# Revit family: IS_Ceratherm50_A6368_BIM_FR
name_source: partatom
category: Plumbing Fixtures
revit_build: Autodesk Revit 2017 (Build: 20160225_1515(x64)
units: mm (PartAtom-declared; Revit-internal decimal feet)

## family parameters
Always vertical = No
Cut with Voids When Loaded = No
OmniClass Number = 23.45.05.17
OmniClass Title = Sanitary Leisure Units
Part Type = Normal
Room Calculation Point = No
Round Connector Dimension = Use Diameter
Shared = No
Work Plane-Based = No

## types (1)
- A6368AA - IDEALRAIN COMBI  DCH TH  L3 3J  90 1,75M CH
    Accessoires = www.idealspec.fr
    Auteur = Ideal Standard
    BIMobject category = Showers
    BIMobject category code = sanitary-showers
    BIMobject main category = Sanitary
    BIMobject main category code = sanitary
    BOSUseNativeGeometries = 1
    Bim-NomDuProjet = ISI_IdealStandard_ShowerHeads_IDEALRAIN_A6368AA
    Brand url = www.idealspec.fr
    Caractéristiques = IDEALRAIN SHR EXP &KIT/I'R 3F 900 NEW
    CodeBarre = 4015413334525
    Conformité = NF
    ConseilsDInstallation = 0
    Cost = 0 $
    Couleur = Chrome
    CoûtDeRemplacement = 0
    Date of publishing = 2018_07_24
    DateDeCréation = 2018_07_24
    Description = IDEALRAIN Ensemble de douche thermostatique
    Dimensions = 1104 x 188 x 436 mm
    EAN code = https://4015413334525
    Edition number = 1
    Espace = Interne
    Finition = Chrome
    Forme = Complexe
    Hauteur = 1104 mm
    IFC Classification = Sanitary Terminal
    IfcExportAs = SHOWERS
    IfcExportType = IfcValveType
    InformationsProduit = www.idealspec.fr
    Installation instructions = http://www.idealspec.fr
    Largeur = 188 mm
    Longueur = 436 mm
    Manufacturer name = Ideal Standard
    Marque = Ideal Standard
    Material main = Brass
    Matériel = Brass
    Model = A6368AA
    NBS Reference Code = 35-06-81
    NBS Reference Description = Shower Heads
    Nominal height = 904
    Nominal width = 304
    OmniClass Code = 23-31 17 00
    OmniClass Description = Showers
    Product Guid = 17cbef67-e42c-4ce9-9d03-9a8c88c3f477
    Product SKU = A6368
    Product certification = http://www.idealspec.fr
    Product data url = https://bimobject.com
    Product family = IDEALRAIN
    Product group = Shower
    Product name = IDEALRAIN SHR EXP &KIT/I'R 3F 900 NEW
    Product url = http://www.idealspec.fr
    Profondeur = 0 mm  [stored 0 ft]
    QR code = http://bimobject.com
    Raccordement = Plomberie
    Révision = 1
    Technical description = http://www.idealspec.fr
    TestDePression = 0
    TypeDeRobinetterie = Shower Mixer
    URL = www.idealspec.fr
    Uniclass 1.4 Code = L7214
    Uniclass 1.4 Description = Showers
    Uniclass 2.0 Code = PR-35-06-81
    Uniclass 2.0 Description = Shower Heads
    Uniclass 2015 Code = Pr_40_20_87_75
    Uniclass 2015 Name = Shower fittings package
    Uniclass2015Code = Pr_40_20_87_75
    Uniclass2015Title = Shower fittings package
    Uniclass2015Version = Products v1.1
    UnitéDeMesure = Millimètres
    UnitéDeTemps = An
    UnitéMonétaire = €
    UrlDuFabricant = www.idealspec.fr
    Version = 1
    Weight Net (Kg) = 3.3
    Youtube clip = http://www.idealspec.fr

note: [stored X ft] marks values corroborated as IEEE doubles in the binary element streams (Revit-internal decimal feet)

## geometry (parser evidence)
native form markers: Sweep x1
no freeform markers — native parametric forms only
